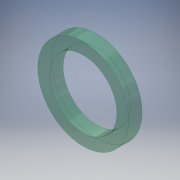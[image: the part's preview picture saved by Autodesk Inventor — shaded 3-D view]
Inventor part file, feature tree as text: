
AUTODESK INVENTOR PART (.ipt)
format: ipt  version: 2019.4 (Build 234330000, 330)  size: 104,960 bytes
history: native  units: mm
features: extrude x1, sketch x1
ambient origin geometry x8: Origin, YZ Plane, XZ Plane, XY Plane, X Axis, Y Axis, Z Axis, Center Point
bodies: Solid1 (feature_tree)
feature tree (2):
  extrude  "Extrusion1"  Depth=4.0mm
  sketch  "Sketch1"  dims[d0=27.0mm d1=20.0mm d2=4.0mm d3=0.0mm]
